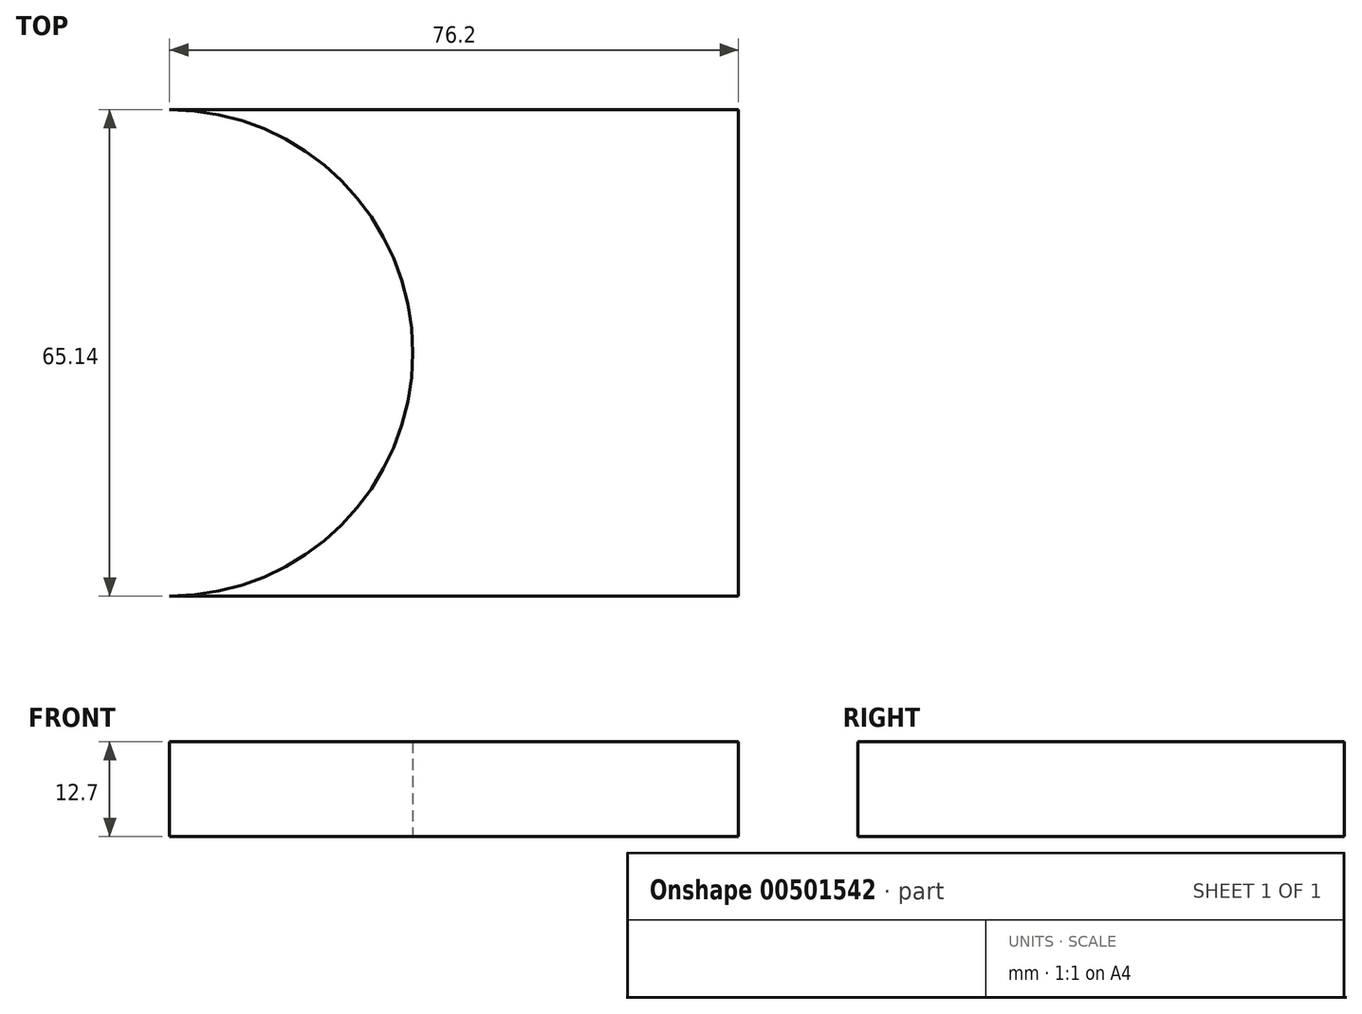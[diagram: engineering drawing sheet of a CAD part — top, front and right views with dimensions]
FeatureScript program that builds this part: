
annotation { "Feature Type Name" : "Feature", "Feature Type Description" : "" }
export const myFeature = defineFeature(function(context is Context, id is Id, definition is map)
    precondition{}
    {
        {
            var Q0;
            Q0=qCreatedBy(makeId("Top.planeOp"),FACE);
            var sketch = newSketch(context, id + "F0", { "sketchPlane" : qUnion([Q0])});
            skLineSegment(sketch, "E0.bottom", {"start": v(-38.1, -32.57) * mm, "end": v(38.1, -32.57) * mm});
            skLineSegment(sketch, "E0.top", {"start": v(-38.1, 32.57) * mm, "end": v(38.1, 32.57) * mm});
            skLineSegment(sketch, "E0.left", {"start": v(-38.1, -32.57) * mm, "end": v(-38.1, 32.57) * mm});
            skLineSegment(sketch, "E0.right", {"start": v(38.1, -32.57) * mm, "end": v(38.1, 32.57) * mm});
            skPoint(sketch, "E0.middle", {"position": v(0, 0) * mm});
            skCircle(sketch, "E1", {"center": v(-38.1, 0) * mm, "radius": 32.57 * mm});
            skCircle(sketch, "E2", {"center": v(-38.1, 0) * mm, "radius": 12.7 * mm});
            skSolve(sketch);
        }
        {
            var Q0;
            {var subQ0=sQuery(id+"F0.wireOp",EDGE,"E0.bottom");Q0=makeQuery(id+"F0.imprint","IMPRINT",FACE,{"disambiguationData":[TD([[makeQuery(id+"F0.imprint","IMPRINT",EDGE,{"derivedFrom":subQ0}),1.0]])]});}
            extrude(context, id + "F1", {"entities" : qUnion([Q0]), "depth" : 12.7 * mm});
        }
    });
